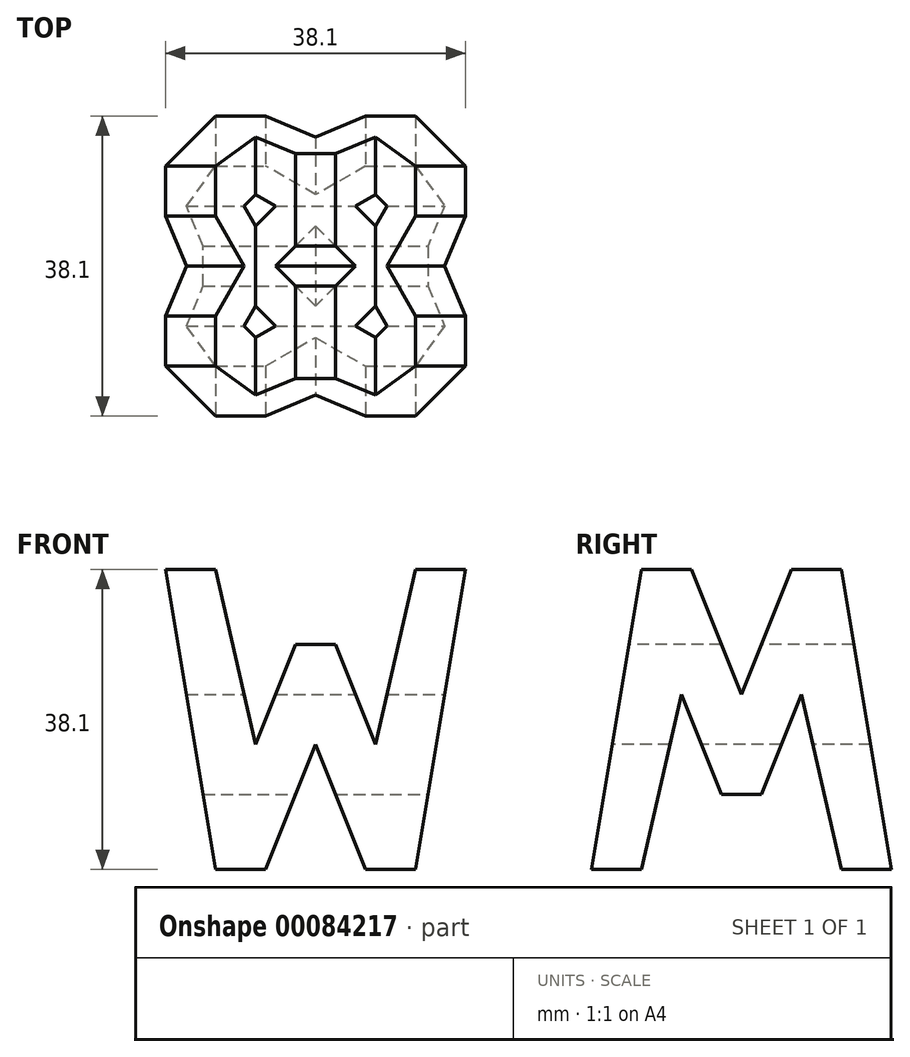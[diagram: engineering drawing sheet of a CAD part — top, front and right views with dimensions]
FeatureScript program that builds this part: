
annotation { "Feature Type Name" : "Feature", "Feature Type Description" : "" }
export const myFeature = defineFeature(function(context is Context, id is Id, definition is map)
    precondition{}
    {
        {
            var Q0;
            Q0=qCreatedBy(makeId("Front.planeOp"),FACE);
            var sketch = newSketch(context, id + "F0", { "sketchPlane" : qUnion([Q0])});
            skLineSegment(sketch, "E0", {"start": v(0, 38.1) * mm, "end": v(38.1, 38.1) * mm});
            skLineSegment(sketch, "E1", {"start": v(38.1, 38.1) * mm, "end": v(38.1, 0) * mm});
            skLineSegment(sketch, "E2", {"start": v(38.1, 0) * mm, "end": v(0, 0) * mm});
            skLineSegment(sketch, "E3", {"start": v(0, 0) * mm, "end": v(0, 38.1) * mm});
            skSolve(sketch);
        }
        {
            var Q0;
            Q0 = qSketchRegion(id + "F0", true);
            extrude(context, id + "F1", {"entities" : qUnion([Q0]), "depth" : 38.1 * mm});
        }
        {
            var Q0;
            Q0=qCreatedBy(makeId("Front.planeOp"),FACE);
            cPlane(context, id + "F2", {"entities" : qUnion([Q0]), "cplaneType" : CPlaneType.OFFSET, "offset" : 38.1 * mm, "width" : 152.4 * mm, "height" : 152.4 * mm});
        }
        {
            var Q0;
            Q0=qCreatedBy(makeId("Right.planeOp"),FACE);
            cPlane(context, id + "F3", {"entities" : qUnion([Q0]), "cplaneType" : CPlaneType.OFFSET, "offset" : 38.1 * mm, "width" : 152.4 * mm, "height" : 152.4 * mm});
        }
        {
            var Q0;
            Q0=qCreatedBy(makeId("Top.planeOp"),FACE);
            cPlane(context, id + "F4", {"entities" : qUnion([Q0]), "cplaneType" : CPlaneType.OFFSET, "offset" : 38.1 * mm, "width" : 152.4 * mm, "height" : 152.4 * mm});
        }
        {
            var Q0;
            Q0=qCreatedBy(id+"F2.planeOp",FACE);
            var sketch = newSketch(context, id + "F5", { "sketchPlane" : qUnion([Q0])});
            skLineSegment(sketch, "E4", {"start": v(6.35, 0) * mm, "end": v(0, 38.1) * mm});
            skLineSegment(sketch, "E5", {"start": v(12.7, 0) * mm, "end": v(19.05, 15.88) * mm});
            skLineSegment(sketch, "E6", {"start": v(19.05, 15.88) * mm, "end": v(25.4, 0) * mm});
            skLineSegment(sketch, "E7", {"start": v(38.1, 38.1) * mm, "end": v(31.75, 0) * mm});
            skLineSegment(sketch, "E8", {"start": v(6.35, 38.1) * mm, "end": v(11.43, 15.88) * mm});
            skLineSegment(sketch, "E9", {"start": v(11.43, 15.88) * mm, "end": v(16.5, 28.58) * mm});
            skLineSegment(sketch, "E10", {"start": v(16.51, 28.58) * mm, "end": v(21.59, 28.58) * mm});
            skLineSegment(sketch, "E11", {"start": v(21.6, 28.57) * mm, "end": v(26.67, 15.88) * mm});
            skLineSegment(sketch, "E12", {"start": v(26.67, 15.88) * mm, "end": v(31.75, 38.1) * mm});
            skLineSegment(sketch, "E13.bottom", {"start": v(0, 0) * mm, "end": v(38.1, 0) * mm});
            skLineSegment(sketch, "E13.top", {"start": v(0, 38.1) * mm, "end": v(38.1, 38.1) * mm});
            skLineSegment(sketch, "E13.left", {"start": v(0, 0) * mm, "end": v(0, 38.1) * mm});
            skLineSegment(sketch, "E13.right", {"start": v(38.1, 0) * mm, "end": v(38.1, 38.1) * mm});
            skSolve(sketch);
        }
        {
            var Q0;
            {var subQ0=sQuery(id+"F5.wireOp",EDGE,"E8");Q0=makeQuery(id+"F5.imprint","IMPRINT",FACE,{"disambiguationData":[TD([[makeQuery(id+"F5.imprint","IMPRINT",EDGE,{"derivedFrom":subQ0}),1.0]])]});}
            var Q1;
            {var subQ0=sQuery(id+"F5.wireOp",EDGE,"E4");Q1=makeQuery(id+"F5.imprint","IMPRINT",FACE,{"disambiguationData":[TD([[makeQuery(id+"F5.imprint","IMPRINT",EDGE,{"derivedFrom":subQ0}),1.0]])]});}
            var Q2;
            {var subQ0=sQuery(id+"F5.wireOp",EDGE,"E5");Q2=makeQuery(id+"F5.imprint","IMPRINT",FACE,{"disambiguationData":[TD([[makeQuery(id+"F5.imprint","IMPRINT",EDGE,{"derivedFrom":subQ0}),-1.0]])]});}
            var Q3;
            {var subQ0=sQuery(id+"F5.wireOp",EDGE,"E7");Q3=makeQuery(id+"F5.imprint","IMPRINT",FACE,{"disambiguationData":[TD([[makeQuery(id+"F5.imprint","IMPRINT",EDGE,{"derivedFrom":subQ0}),1.0]])]});}
            extrude(context, id + "F6", {"entities" : qUnion([Q0, Q1, Q2, Q3]), "operationType" : NewBodyOperationType.REMOVE, "oppositeDirection" : true, "depth" : 38.1 * mm});
        }
        {
            var Q0;
            Q0=qCreatedBy(id+"F3.planeOp",FACE);
            var sketch = newSketch(context, id + "F7", { "sketchPlane" : qUnion([Q0])});
            skLineSegment(sketch, "E14", {"start": v(-38.1, 38.1) * mm, "end": v(-38.1, 0) * mm});
            skLineSegment(sketch, "E15", {"start": v(-38.1, 0) * mm, "end": v(0, 0) * mm});
            skLineSegment(sketch, "E16", {"start": v(0, 0) * mm, "end": v(0, 38.1) * mm});
            skLineSegment(sketch, "E17", {"start": v(0, 38.1) * mm, "end": v(-38.1, 38.1) * mm});
            skLineSegment(sketch, "E18", {"start": v(-38.1, 38.1) * mm, "end": v(0, 38.1) * mm});
            skLineSegment(sketch, "E19", {"start": v(-31.75, 38.1) * mm, "end": v(-38.1, 0) * mm});
            skLineSegment(sketch, "E20", {"start": v(-31.75, 0) * mm, "end": v(-26.67, 22.22) * mm});
            skLineSegment(sketch, "E21", {"start": v(-26.67, 22.22) * mm, "end": v(-21.59, 9.53) * mm});
            skLineSegment(sketch, "E22", {"start": v(-21.59, 9.53) * mm, "end": v(-16.5, 9.53) * mm});
            skLineSegment(sketch, "E23", {"start": v(-16.5, 9.53) * mm, "end": v(-11.43, 22.22) * mm});
            skLineSegment(sketch, "E24", {"start": v(-11.43, 22.22) * mm, "end": v(-6.35, 0) * mm});
            skLineSegment(sketch, "E25", {"start": v(-25.4, 38.1) * mm, "end": v(-19.05, 22.23) * mm});
            skLineSegment(sketch, "E26", {"start": v(-19.05, 22.23) * mm, "end": v(-12.7, 38.1) * mm});
            skLineSegment(sketch, "E27", {"start": v(-6.35, 38.1) * mm, "end": v(0, 0) * mm});
            skSolve(sketch);
        }
        {
            var Q0;
            {var subQ0=sQuery(id+"F7.wireOp",EDGE,"E20");Q0=makeQuery(id+"F7.imprint","IMPRINT",FACE,{"disambiguationData":[TD([[makeQuery(id+"F7.imprint","IMPRINT",EDGE,{"derivedFrom":subQ0}),-1.0]])]});}
            var Q1;
            {var subQ0=sQuery(id+"F7.wireOp",EDGE,"E14");Q1=makeQuery(id+"F7.imprint","IMPRINT",FACE,{"disambiguationData":[TD([[makeQuery(id+"F7.imprint","IMPRINT",EDGE,{"derivedFrom":subQ0}),1.0]])]});}
            var Q2;
            {var subQ0=sQuery(id+"F7.wireOp",EDGE,"E16");Q2=makeQuery(id+"F7.imprint","IMPRINT",FACE,{"disambiguationData":[TD([[makeQuery(id+"F7.imprint","IMPRINT",EDGE,{"derivedFrom":subQ0}),1.0]])]});}
            var Q3;
            {var subQ0=sQuery(id+"F7.wireOp",EDGE,"E25");Q3=makeQuery(id+"F7.imprint","IMPRINT",FACE,{"disambiguationData":[TD([[makeQuery(id+"F7.imprint","IMPRINT",EDGE,{"derivedFrom":subQ0}),1.0]])]});}
            extrude(context, id + "F8", {"entities" : qUnion([Q0, Q1, Q2, Q3]), "operationType" : NewBodyOperationType.REMOVE, "oppositeDirection" : true, "depth" : 38.1 * mm});
        }
    });
